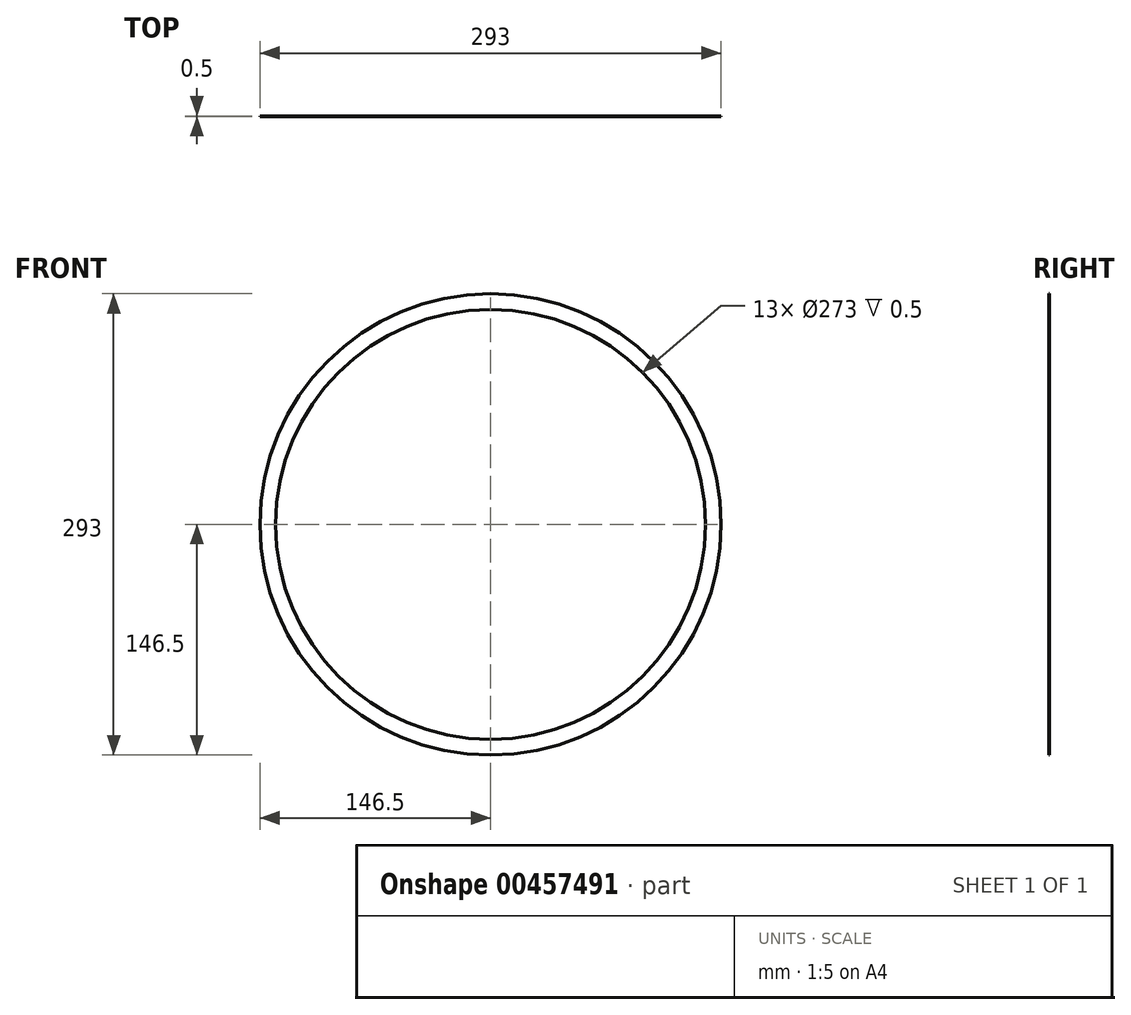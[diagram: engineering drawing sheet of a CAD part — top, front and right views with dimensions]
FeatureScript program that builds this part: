
annotation { "Feature Type Name" : "Feature", "Feature Type Description" : "" }
export const myFeature = defineFeature(function(context is Context, id is Id, definition is map)
    precondition{}
    {
        {
            var Q0;
            Q0=qCreatedBy(makeId("Front.planeOp"),FACE);
            var sketch = newSketch(context, id + "F0", { "sketchPlane" : qUnion([Q0])});
            skCircle(sketch, "E0", {"center": v(0, 0) * mm, "radius": 146.5 * mm});
            skCircle(sketch, "E1", {"center": v(0, 0) * mm, "radius": 136.5 * mm});
            skSolve(sketch);
        }
        {
            var Q0;
            Q0=makeQuery(id+"F0.imprint","IMPRINT",FACE,{"disambiguationData":[TD([[makeQuery(id+"F0.imprint","IMPRINT",EDGE,{"derivedFrom":sQuery(id+"F0.wireOp",EDGE,"E0")}),1.0]])]});
            extrude(context, id + "F1", {"entities" : qUnion([Q0]), "depth" : 0.5 * mm});
        }
    });
